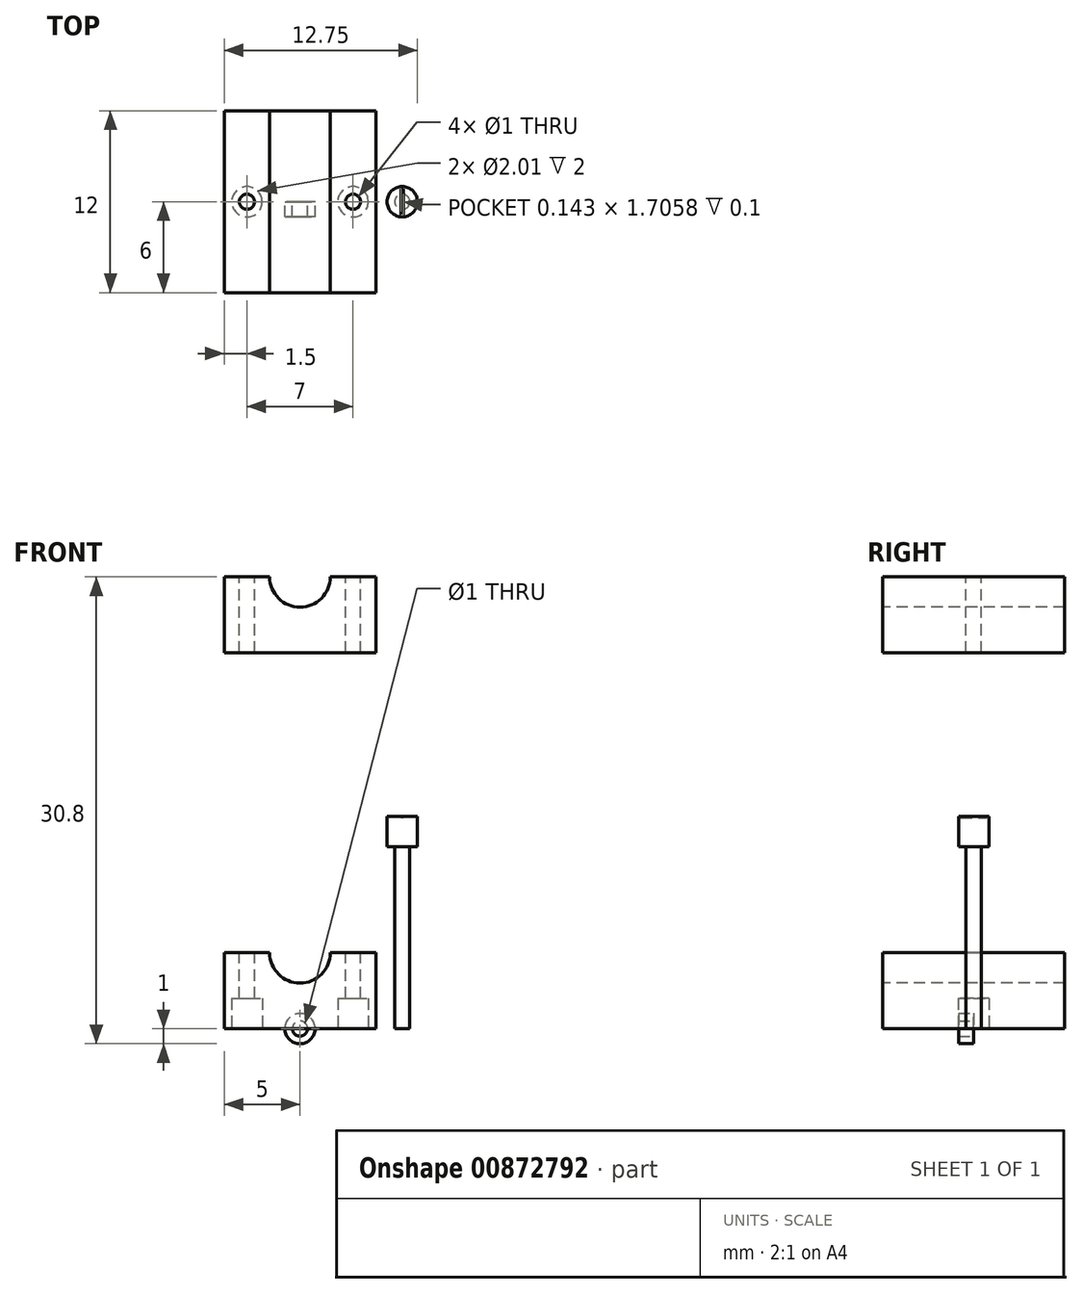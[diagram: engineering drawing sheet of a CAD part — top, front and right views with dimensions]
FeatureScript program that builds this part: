
annotation { "Feature Type Name" : "Feature", "Feature Type Description" : "" }
export const myFeature = defineFeature(function(context is Context, id is Id, definition is map)
    precondition{}
    {
        {
            var Q0;
            Q0=qCreatedBy(makeId("Top.planeOp"),FACE);
            var sketch = newSketch(context, id + "F0", { "sketchPlane" : qUnion([Q0])});
            skLineSegment(sketch, "E0.bottom", {"start": v(5, -6) * mm, "end": v(-5, -6) * mm});
            skLineSegment(sketch, "E0.top", {"start": v(5, 6) * mm, "end": v(-5, 6) * mm});
            skLineSegment(sketch, "E0.left", {"start": v(5, -6) * mm, "end": v(5, 6) * mm});
            skLineSegment(sketch, "E0.right", {"start": v(-5, -6) * mm, "end": v(-5, 6) * mm});
            skPoint(sketch, "E0.middle", {"position": v(0, 0) * mm});
            skSolve(sketch);
        }
        {
            var Q0;
            Q0=qSketchRegion(id+"F0",true);
            extrude(context, id + "F1", {"entities" : qUnion([Q0]), "depth" : 5 * mm, "offsetDistance" : 25 * mm});
        }
        {
            var Q0;
            Q0=makeQuery(id+"F1.opExtrude","SWEPT_FACE",FACE,{"disambiguationData":[OSD([sQuery(id+"F0.wireOp",EDGE,"E0.bottom")])]});
            var sketch = newSketch(context, id + "F2", { "sketchPlane" : qUnion([Q0])});
            skArc(sketch, "E1", {"start": v(-2, 5) * mm, "mid": v(0, 3) * mm, "end": v(2, 5) * mm});
            skLineSegment(sketch, "E2", {"start": v(-2, 5) * mm, "end": v(2, 5) * mm});
            skSolve(sketch);
        }
        {
            var Q0;
            Q0=qSketchRegion(id+"F2",true);
            extrude(context, id + "F3", {"entities" : qUnion([Q0]), "operationType" : NewBodyOperationType.REMOVE, "endBound" : BoundingType.THROUGH_ALL, "oppositeDirection" : true, "depth" : 25 * mm, "offsetDistance" : 25 * mm});
        }
        {
            var Q0;
            {var subQ0=sQuery(id+"F0.wireOp",EDGE,"E0.bottom");var subQ1=sQuery(id+"F0.wireOp",EDGE,"E0.right");var subQ2=sQuery(id+"F0.wireOp",EDGE,"E0.top");Q0=makeQuery(id+"F3.boolean.opBoolean","SPLIT",FACE,{"disambiguationData":[TD([makeQuery(id+"F1.opExtrude","SWEPT_FACE",FACE,{"disambiguationData":[OSD([subQ1])]})])],"derivedFrom":makeQuery(id+"F1.opExtrude","CAP_FACE",FACE,{"disambiguationData":[OSD([subQ0,subQ2,sQuery(id+"F0.wireOp",EDGE,"E0.left"),subQ1])],"isStart":false})});}
            var sketch = newSketch(context, id + "F4", { "sketchPlane" : qUnion([Q0])});
            skCircle(sketch, "E3", {"center": v(-3.5, 0) * mm, "radius": 0.5 * mm});
            skSolve(sketch);
        }
        {
            var Q0;
            {var subQ0=sQuery(id+"F0.wireOp",EDGE,"E0.bottom");var subQ1=sQuery(id+"F0.wireOp",EDGE,"E0.top");var subQ2=sQuery(id+"F0.wireOp",EDGE,"E0.left");Q0=makeQuery(id+"F3.boolean.opBoolean","SPLIT",FACE,{"disambiguationData":[TD([makeQuery(id+"F1.opExtrude","SWEPT_FACE",FACE,{"disambiguationData":[OSD([subQ2])]})])],"derivedFrom":makeQuery(id+"F1.opExtrude","CAP_FACE",FACE,{"disambiguationData":[OSD([subQ0,subQ1,subQ2,sQuery(id+"F0.wireOp",EDGE,"E0.right")])],"isStart":false})});}
            var sketch = newSketch(context, id + "F5", { "sketchPlane" : qUnion([Q0])});
            skCircle(sketch, "E4", {"center": v(3.5, 0) * mm, "radius": 0.5 * mm});
            skSolve(sketch);
        }
        {
            var Q0;
            Q0=qSketchRegion(id+"F4",true);
            extrude(context, id + "F6", {"entities" : qUnion([Q0]), "operationType" : NewBodyOperationType.REMOVE, "endBound" : BoundingType.THROUGH_ALL, "oppositeDirection" : true, "depth" : 25 * mm, "offsetDistance" : 25 * mm});
        }
        {
            var Q0;
            Q0=makeQuery(id+"F5.imprint","IMPRINT",FACE,{"disambiguationData":[TD([[makeQuery(id+"F5.imprint","IMPRINT",EDGE,{"derivedFrom":sQuery(id+"F5.wireOp",EDGE,"E4")}),1.0]])]});
            extrude(context, id + "F7", {"entities" : qUnion([Q0]), "operationType" : NewBodyOperationType.REMOVE, "endBound" : BoundingType.THROUGH_ALL, "oppositeDirection" : true, "depth" : 25 * mm, "offsetDistance" : 25 * mm});
        }
        {
            var Q0;
            Q0=qCreatedBy(makeId("Top.planeOp"),FACE);
            var sketch = newSketch(context, id + "F8", { "sketchPlane" : qUnion([Q0])});
            skCircle(sketch, "E5", {"center": v(6.75, 0) * mm, "radius": 0.5 * mm});
            skSolve(sketch);
        }
        {
            var Q0;
            Q0=qSketchRegion(id+"F8",true);
            extrude(context, id + "F9", {"entities" : qUnion([Q0]), "depth" : 12 * mm, "offsetDistance" : 25 * mm});
        }
        {
            var Q0;
            Q0=makeQuery(id+"F9.opExtrude","CAP_FACE",FACE,{"disambiguationData":[OSD([sQuery(id+"F8.wireOp",EDGE,"E5")])],"isStart":false});
            var sketch = newSketch(context, id + "F10", { "sketchPlane" : qUnion([Q0])});
            skCircle(sketch, "E6", {"center": v(6.75, 0) * mm, "radius": 1 * mm});
            skSolve(sketch);
        }
        {
            var Q0;
            Q0=qSketchRegion(id+"F10",true);
            extrude(context, id + "F11", {"entities" : qUnion([Q0]), "operationType" : NewBodyOperationType.ADD, "depth" : 2 * mm, "offsetDistance" : 25 * mm});
        }
        {
            var Q0;
            Q0=qCreatedBy(makeId("Front.planeOp"),FACE);
            var sketch = newSketch(context, id + "F12", { "sketchPlane" : qUnion([Q0])});
            skCircle(sketch, "E7", {"center": v(0, 0) * mm, "radius": 0.5 * mm});
            skCircle(sketch, "E8", {"center": v(0, 0) * mm, "radius": 1 * mm});
            skSolve(sketch);
        }
        {
            var Q0;
            Q0=qSketchRegion(id+"F12",true);
            extrude(context, id + "F13", {"entities" : qUnion([Q0]), "depth" : 1 * mm, "offsetDistance" : 25 * mm});
        }
        {
            var Q0;
            Q0=makeQuery(id+"F1.opExtrude","SWEPT_BODY",BODY,{"disambiguationData":[OSD([sQuery(id+"F0.wireOp",EDGE,"E0.bottom"),sQuery(id+"F0.wireOp",EDGE,"E0.top"),sQuery(id+"F0.wireOp",EDGE,"E0.left"),sQuery(id+"F0.wireOp",EDGE,"E0.right")])]});
            transform(context, id + "F14", {"entities" : qUnion([Q0]), "transformType" : TransformType.TRANSLATION_3D, "dx" : 0 * mm, "dy" : 0 * mm, "dz" : 24.8 * mm, "makeCopy" : true});
        }
        {
            var Q0;
            Q0=makeQuery(id+"F1.opExtrude","CAP_FACE",FACE,{"disambiguationData":[OSD([sQuery(id+"F0.wireOp",EDGE,"E0.bottom"),sQuery(id+"F0.wireOp",EDGE,"E0.top"),sQuery(id+"F0.wireOp",EDGE,"E0.left"),sQuery(id+"F0.wireOp",EDGE,"E0.right")])],"isStart":true});
            var sketch = newSketch(context, id + "F15", { "sketchPlane" : qUnion([Q0])});
            skCircle(sketch, "E9", {"center": v(-3.5, 0) * mm, "radius": 1 * mm});
            skCircle(sketch, "E10", {"center": v(3.5, 0) * mm, "radius": 1 * mm});
            skSolve(sketch);
        }
        {
            var Q0;
            Q0=qSketchRegion(id+"F15",true);
            extrude(context, id + "F16", {"entities" : qUnion([Q0]), "operationType" : NewBodyOperationType.REMOVE, "oppositeDirection" : true, "depth" : 2 * mm, "offsetDistance" : 25 * mm});
        }
        {
            var Q0;
            Q0=makeQuery(id+"F11.opExtrude","CAP_FACE",FACE,{"disambiguationData":[OSD([sQuery(id+"F10.wireOp",EDGE,"E6")])],"isStart":false});
            var sketch = newSketch(context, id + "F17", { "sketchPlane" : qUnion([Q0])});
            skLineSegment(sketch, "E11.bottom", {"start": v(6.82, -0.85) * mm, "end": v(6.67, -0.85) * mm});
            skLineSegment(sketch, "E11.top", {"start": v(6.82, 0.85) * mm, "end": v(6.67, 0.85) * mm});
            skLineSegment(sketch, "E11.left", {"start": v(6.82, -0.85) * mm, "end": v(6.82, 0.85) * mm});
            skLineSegment(sketch, "E11.right", {"start": v(6.67, -0.85) * mm, "end": v(6.67, 0.85) * mm});
            skPoint(sketch, "E11.middle", {"position": v(6.75, 0) * mm});
            skSolve(sketch);
        }
        {
            var Q0;
            Q0=qSketchRegion(id+"F17",true);
            extrude(context, id + "F18", {"entities" : qUnion([Q0]), "operationType" : NewBodyOperationType.REMOVE, "oppositeDirection" : true, "depth" : 0.1 * mm, "offsetDistance" : 25 * mm});
        }
    });
